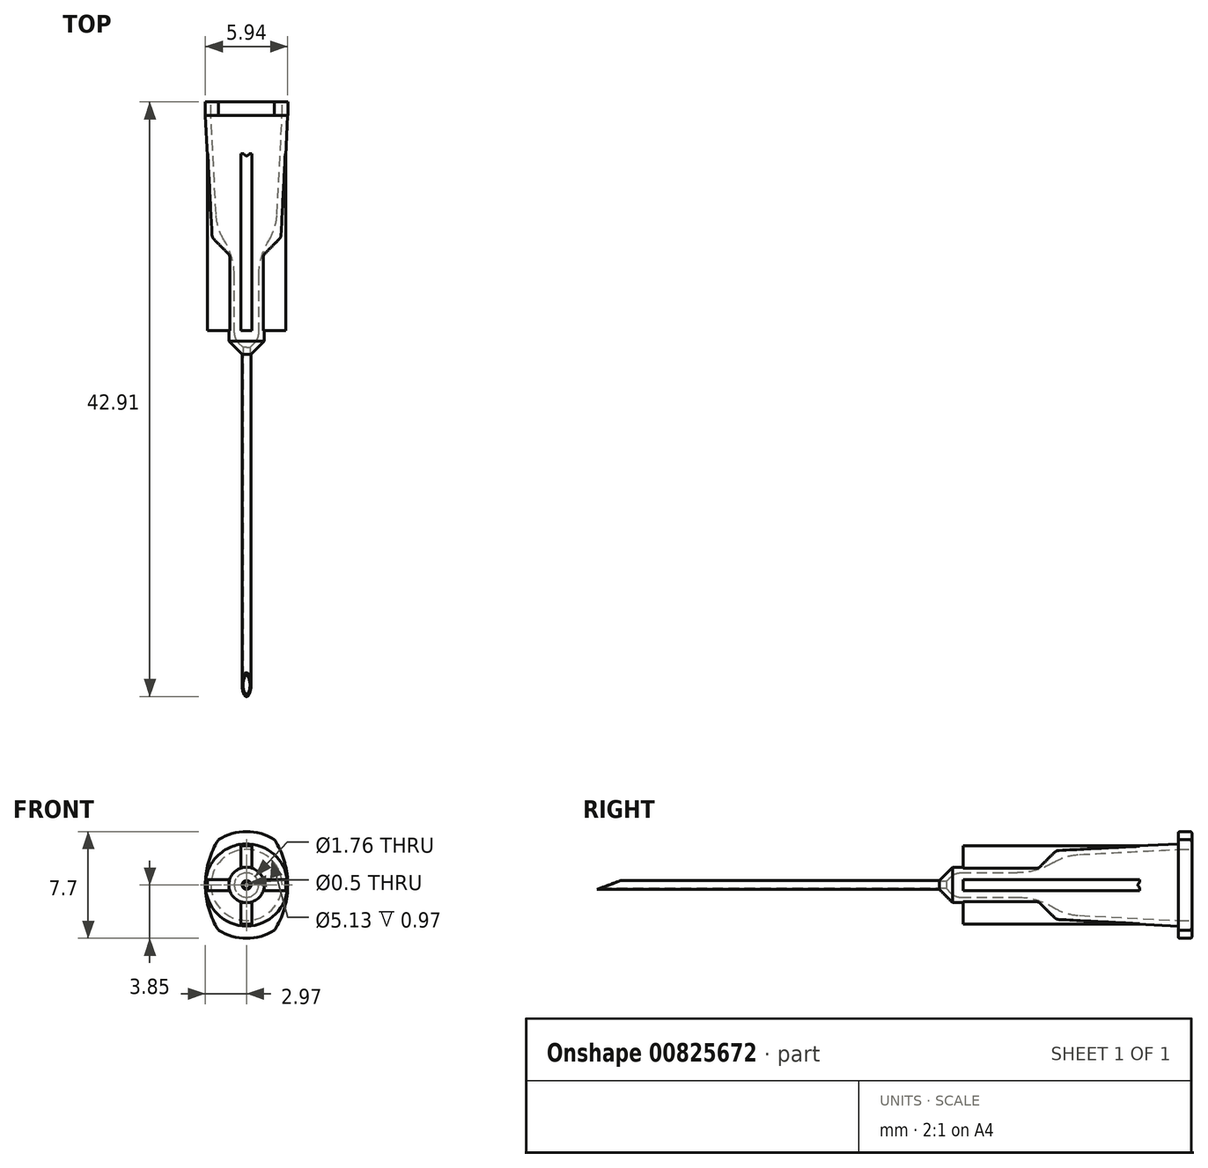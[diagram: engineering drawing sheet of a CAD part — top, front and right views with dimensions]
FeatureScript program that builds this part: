
annotation { "Feature Type Name" : "Feature", "Feature Type Description" : "" }
export const myFeature = defineFeature(function(context is Context, id is Id, definition is map)
    precondition{}
    {
        {
            var Q0;
            Q0=qCreatedBy(makeId("Front.planeOp"),FACE);
            var sketch = newSketch(context, id + "F0", { "sketchPlane" : qUnion([Q0])});
            skCircle(sketch, "E0", {"center": v(0, 0) * mm, "radius": 2.97 * mm});
            skSolve(sketch);
        }
        {
            var Q0;
            Q0=qCreatedBy(makeId("Front.planeOp"),FACE);
            cPlane(context, id + "F1", {"entities" : qUnion([Q0]), "cplaneType" : CPlaneType.OFFSET, "offset" : 8.8 * mm, "width" : 150 * mm, "height" : 150 * mm});
        }
        {
            var Q0;
            Q0=qCreatedBy(id+"F1.planeOp",FACE);
            var sketch = newSketch(context, id + "F2", { "sketchPlane" : qUnion([Q0])});
            skCircle(sketch, "E1", {"center": v(0, 0) * mm, "radius": 2.52 * mm});
            skSolve(sketch);
        }
        {
            var Q0;
            Q0=makeQuery(id+"F0.imprint","IMPRINT",FACE,{"disambiguationData":[TD([[makeQuery(id+"F0.imprint","IMPRINT",EDGE,{"derivedFrom":sQuery(id+"F0.wireOp",EDGE,"E0")}),1.0]])]});
            var Q1;
            Q1=makeQuery(id+"F2.imprint","IMPRINT",FACE,{"disambiguationData":[TD([[makeQuery(id+"F2.imprint","IMPRINT",EDGE,{"derivedFrom":sQuery(id+"F2.wireOp",EDGE,"E1")}),1.0]])]});
            loft(context, id + "F3", {"sheetProfilesArray" : [{ "sheetProfileEntities" : qUnion([Q0]) }, { "sheetProfileEntities" : qUnion([Q1]) }]});
        }
        {
            var Q0;
            Q0=makeQuery(id+"F3.opLoft","CAP_FACE",FACE,{"disambiguationData":[OSD([makeQuery(id+"F2.imprint","IMPRINT",FACE,{"disambiguationData":[TD([[makeQuery(id+"F2.imprint","IMPRINT",EDGE,{"derivedFrom":sQuery(id+"F2.wireOp",EDGE,"E1")}),1.0]])]})])],"isStart":true});
            cPlane(context, id + "F4", {"entities" : qUnion([Q0]), "cplaneType" : CPlaneType.OFFSET, "offset" : 1.28 * mm, "width" : 150 * mm, "height" : 150 * mm});
        }
        {
            var Q0;
            Q0=qCreatedBy(id+"F4.planeOp",FACE);
            var sketch = newSketch(context, id + "F5", { "sketchPlane" : qUnion([Q0])});
            skCircle(sketch, "E2", {"center": v(0, 0) * mm, "radius": 1.28 * mm});
            skSolve(sketch);
        }
        {
            var Q1;
            Q1=makeQuery(id+"F3.opLoft","CAP_FACE",FACE,{"disambiguationData":[OSD([makeQuery(id+"F2.imprint","IMPRINT",FACE,{"disambiguationData":[TD([[makeQuery(id+"F2.imprint","IMPRINT",EDGE,{"derivedFrom":sQuery(id+"F2.wireOp",EDGE,"E1")}),1.0]])]})])],"isStart":true});
            var Q2;
            Q2=makeQuery(id+"F5.imprint","IMPRINT",FACE,{"disambiguationData":[TD([[makeQuery(id+"F5.imprint","IMPRINT",EDGE,{"derivedFrom":sQuery(id+"F5.wireOp",EDGE,"E2")}),1.0]])]});
            loft(context, id + "F6", {"operationType" : NewBodyOperationType.ADD, "sheetProfilesArray" : [{ "sheetProfileEntities" : qUnion([Q1]) }, { "sheetProfileEntities" : qUnion([Q2]) }]});
        }
        {
            var Q0;
            Q0=makeQuery(id+"F6.opLoft","CAP_FACE",FACE,{"disambiguationData":[OSD([makeQuery(id+"F5.imprint","IMPRINT",FACE,{"disambiguationData":[TD([[makeQuery(id+"F5.imprint","IMPRINT",EDGE,{"derivedFrom":sQuery(id+"F5.wireOp",EDGE,"E2")}),1.0]])]})])],"isStart":true});
            extrude(context, id + "F7", {"entities" : qUnion([Q0]), "operationType" : NewBodyOperationType.ADD, "depth" : 6.2 * mm, "offsetDistance" : 25 * mm});
        }
        {
            var Q0;
            Q0=makeQuery(id+"F7.opExtrude","CAP_FACE",FACE,{"disambiguationData":[OSD([makeQuery(id+"F5.imprint","IMPRINT",FACE,{"disambiguationData":[TD([[makeQuery(id+"F5.imprint","IMPRINT",EDGE,{"derivedFrom":sQuery(id+"F5.wireOp",EDGE,"E2")}),1.0]])]})])],"isStart":false});
            var sketch = newSketch(context, id + "F8", { "sketchPlane" : qUnion([Q0])});
            skLineSegment(sketch, "E3.bottom", {"start": v(0.4, 2.82) * mm, "end": v(-0.4, 2.82) * mm});
            skLineSegment(sketch, "E3.left", {"start": v(0.4, 2.82) * mm, "end": v(0.4, 1.22) * mm});
            skLineSegment(sketch, "E3.right", {"start": v(-0.4, 2.82) * mm, "end": v(-0.4, 1.22) * mm});
            skPoint(sketch, "E3.middle", {"position": v(0, 1.28) * mm});
            skArc(sketch, "E4", {"start": v(0.4, 1.22) * mm, "mid": v(0, 1.28) * mm, "end": v(-0.4, 1.22) * mm});
            skLineSegment(sketch, "E5.1.0", {"start": v(-2.82, -0.4) * mm, "end": v(-1.22, -0.4) * mm});
            skLineSegment(sketch, "E5.1.1", {"start": v(-2.82, 0.4) * mm, "end": v(-1.22, 0.4) * mm});
            skLineSegment(sketch, "E5.1.2", {"start": v(-2.82, 0.4) * mm, "end": v(-2.82, -0.4) * mm});
            skArc(sketch, "E5.1.3", {"start": v(-1.22, 0.4) * mm, "mid": v(-1.28, 0) * mm, "end": v(-1.22, -0.4) * mm});
            skLineSegment(sketch, "E5.2.0", {"start": v(0.4, -2.82) * mm, "end": v(0.4, -1.22) * mm});
            skLineSegment(sketch, "E5.2.1", {"start": v(-0.4, -2.82) * mm, "end": v(-0.4, -1.22) * mm});
            skLineSegment(sketch, "E5.2.2", {"start": v(-0.4, -2.82) * mm, "end": v(0.4, -2.82) * mm});
            skArc(sketch, "E5.2.3", {"start": v(-0.4, -1.22) * mm, "mid": v(0, -1.28) * mm, "end": v(0.4, -1.22) * mm});
            skLineSegment(sketch, "E5.3.0", {"start": v(2.82, 0.4) * mm, "end": v(1.22, 0.4) * mm});
            skLineSegment(sketch, "E5.3.1", {"start": v(2.82, -0.4) * mm, "end": v(1.22, -0.4) * mm});
            skLineSegment(sketch, "E5.3.2", {"start": v(2.82, -0.4) * mm, "end": v(2.82, 0.4) * mm});
            skArc(sketch, "E5.3.3", {"start": v(1.22, -0.4) * mm, "mid": v(1.28, 0) * mm, "end": v(1.22, 0.4) * mm});
            skSolve(sketch);
        }
        {
            var Q0;
            Q0 = qSketchRegion(id + "F8", true);
            extrude(context, id + "F9", {"entities" : qUnion([Q0]), "operationType" : NewBodyOperationType.ADD, "oppositeDirection" : true, "depth" : 13.5 * mm, "offsetDistance" : 25 * mm});
        }
        {
            var Q0;
            Q0=makeQuery(id+"F9.boolean.opBoolean","MERGE",FACE,{"derivedFrom":[makeQuery(id+"F7.opExtrude","CAP_FACE",FACE,{"disambiguationData":[OSD([makeQuery(id+"F5.imprint","IMPRINT",FACE,{"disambiguationData":[TD([[makeQuery(id+"F5.imprint","IMPRINT",EDGE,{"derivedFrom":sQuery(id+"F5.wireOp",EDGE,"E2")}),1.0]])]})])],"isStart":false}),makeQuery(id+"F9.opExtrude","CAP_FACE",FACE,{"disambiguationData":[OSD([sQuery(id+"F8.wireOp",EDGE,"E3.bottom"),sQuery(id+"F8.wireOp",EDGE,"E3.left"),sQuery(id+"F8.wireOp",EDGE,"E3.right"),sQuery(id+"F8.wireOp",EDGE,"E4")])],"isStart":true}),makeQuery(id+"F9.opExtrude","CAP_FACE",FACE,{"disambiguationData":[OSD([sQuery(id+"F8.wireOp",EDGE,"E5.1.0"),sQuery(id+"F8.wireOp",EDGE,"E5.1.1"),sQuery(id+"F8.wireOp",EDGE,"E5.1.2"),sQuery(id+"F8.wireOp",EDGE,"E5.1.3")])],"isStart":true}),makeQuery(id+"F9.opExtrude","CAP_FACE",FACE,{"disambiguationData":[OSD([sQuery(id+"F8.wireOp",EDGE,"E5.2.0"),sQuery(id+"F8.wireOp",EDGE,"E5.2.1"),sQuery(id+"F8.wireOp",EDGE,"E5.2.2"),sQuery(id+"F8.wireOp",EDGE,"E5.2.3")])],"isStart":true}),makeQuery(id+"F9.opExtrude","CAP_FACE",FACE,{"disambiguationData":[OSD([sQuery(id+"F8.wireOp",EDGE,"E5.3.0"),sQuery(id+"F8.wireOp",EDGE,"E5.3.1"),sQuery(id+"F8.wireOp",EDGE,"E5.3.2"),sQuery(id+"F8.wireOp",EDGE,"E5.3.3")])],"isStart":true})]});
            var sketch = newSketch(context, id + "F10", { "sketchPlane" : qUnion([Q0])});
            skLineSegment(sketch, "E6", {"start": v(-0.4, 1.22) * mm, "end": v(-0.4, 2.82) * mm});
            skLineSegment(sketch, "E7", {"start": v(-0.4, 2.82) * mm, "end": v(0.4, 2.82) * mm});
            skLineSegment(sketch, "E8", {"start": v(0.4, 2.82) * mm, "end": v(0.4, 1.22) * mm});
            skArc(sketch, "E9", {"start": v(0.4, 1.22) * mm, "mid": v(0, 1.28) * mm, "end": v(-0.4, 1.22) * mm});
            skLineSegment(sketch, "E10.1.0", {"start": v(-1.22, -0.4) * mm, "end": v(-2.82, -0.4) * mm});
            skArc(sketch, "E10.1.1", {"start": v(-1.22, 0.4) * mm, "mid": v(-1.28, 0) * mm, "end": v(-1.22, -0.4) * mm});
            skLineSegment(sketch, "E10.1.2", {"start": v(-2.82, 0.4) * mm, "end": v(-1.22, 0.4) * mm});
            skLineSegment(sketch, "E10.1.3", {"start": v(-2.82, -0.4) * mm, "end": v(-2.82, 0.4) * mm});
            skLineSegment(sketch, "E10.2.0", {"start": v(0.4, -1.22) * mm, "end": v(0.4, -2.82) * mm});
            skArc(sketch, "E10.2.1", {"start": v(-0.4, -1.22) * mm, "mid": v(0, -1.28) * mm, "end": v(0.4, -1.22) * mm});
            skLineSegment(sketch, "E10.2.2", {"start": v(-0.4, -2.82) * mm, "end": v(-0.4, -1.22) * mm});
            skLineSegment(sketch, "E10.2.3", {"start": v(0.4, -2.82) * mm, "end": v(-0.4, -2.82) * mm});
            skLineSegment(sketch, "E10.3.0", {"start": v(1.22, 0.4) * mm, "end": v(2.82, 0.4) * mm});
            skArc(sketch, "E10.3.1", {"start": v(1.22, -0.4) * mm, "mid": v(1.28, 0) * mm, "end": v(1.22, 0.4) * mm});
            skLineSegment(sketch, "E10.3.2", {"start": v(2.82, -0.4) * mm, "end": v(1.22, -0.4) * mm});
            skLineSegment(sketch, "E10.3.3", {"start": v(2.82, 0.4) * mm, "end": v(2.82, -0.4) * mm});
            skSolve(sketch);
        }
        {
            var Q0;
            Q0 = qSketchRegion(id + "F10", true);
            extrude(context, id + "F11", {"entities" : qUnion([Q0]), "operationType" : NewBodyOperationType.REMOVE, "oppositeDirection" : true, "depth" : .75 * mm, "offsetDistance" : 25 * mm});
        }
        {
            var Q0;
            Q0=makeQuery(id+"F9.boolean.opBoolean","MERGE",FACE,{"derivedFrom":[makeQuery(id+"F7.opExtrude","CAP_FACE",FACE,{"disambiguationData":[OSD([makeQuery(id+"F5.imprint","IMPRINT",FACE,{"disambiguationData":[TD([[makeQuery(id+"F5.imprint","IMPRINT",EDGE,{"derivedFrom":sQuery(id+"F5.wireOp",EDGE,"E2")}),1.0]])]})])],"isStart":false}),makeQuery(id+"F9.opExtrude","CAP_FACE",FACE,{"disambiguationData":[OSD([sQuery(id+"F8.wireOp",EDGE,"E3.bottom"),sQuery(id+"F8.wireOp",EDGE,"E3.left"),sQuery(id+"F8.wireOp",EDGE,"E3.right"),sQuery(id+"F8.wireOp",EDGE,"E4")])],"isStart":true}),makeQuery(id+"F9.opExtrude","CAP_FACE",FACE,{"disambiguationData":[OSD([sQuery(id+"F8.wireOp",EDGE,"E5.1.0"),sQuery(id+"F8.wireOp",EDGE,"E5.1.1"),sQuery(id+"F8.wireOp",EDGE,"E5.1.2"),sQuery(id+"F8.wireOp",EDGE,"E5.1.3")])],"isStart":true}),makeQuery(id+"F9.opExtrude","CAP_FACE",FACE,{"disambiguationData":[OSD([sQuery(id+"F8.wireOp",EDGE,"E5.2.0"),sQuery(id+"F8.wireOp",EDGE,"E5.2.1"),sQuery(id+"F8.wireOp",EDGE,"E5.2.2"),sQuery(id+"F8.wireOp",EDGE,"E5.2.3")])],"isStart":true}),makeQuery(id+"F9.opExtrude","CAP_FACE",FACE,{"disambiguationData":[OSD([sQuery(id+"F8.wireOp",EDGE,"E5.3.0"),sQuery(id+"F8.wireOp",EDGE,"E5.3.1"),sQuery(id+"F8.wireOp",EDGE,"E5.3.2"),sQuery(id+"F8.wireOp",EDGE,"E5.3.3")])],"isStart":true})]});
            cPlane(context, id + "F12", {"entities" : qUnion([Q0]), "cplaneType" : CPlaneType.OFFSET, "offset" : .96 * mm, "width" : 150 * mm, "height" : 150 * mm});
        }
        {
            var Q0;
            Q0=qCreatedBy(id+"F12.planeOp",FACE);
            var sketch = newSketch(context, id + "F13", { "sketchPlane" : qUnion([Q0])});
            skCircle(sketch, "E11", {"center": v(0, 0) * mm, "radius": 0.33 * mm});
            skSolve(sketch);
        }
        {
            var Q1;
            Q1=makeQuery(id+"F9.boolean.opBoolean","MERGE",FACE,{"derivedFrom":[makeQuery(id+"F7.opExtrude","CAP_FACE",FACE,{"disambiguationData":[OSD([makeQuery(id+"F5.imprint","IMPRINT",FACE,{"disambiguationData":[TD([[makeQuery(id+"F5.imprint","IMPRINT",EDGE,{"derivedFrom":sQuery(id+"F5.wireOp",EDGE,"E2")}),1.0]])]})])],"isStart":false}),makeQuery(id+"F9.opExtrude","CAP_FACE",FACE,{"disambiguationData":[OSD([sQuery(id+"F8.wireOp",EDGE,"E3.bottom"),sQuery(id+"F8.wireOp",EDGE,"E3.left"),sQuery(id+"F8.wireOp",EDGE,"E3.right"),sQuery(id+"F8.wireOp",EDGE,"E4")])],"isStart":true}),makeQuery(id+"F9.opExtrude","CAP_FACE",FACE,{"disambiguationData":[OSD([sQuery(id+"F8.wireOp",EDGE,"E5.1.0"),sQuery(id+"F8.wireOp",EDGE,"E5.1.1"),sQuery(id+"F8.wireOp",EDGE,"E5.1.2"),sQuery(id+"F8.wireOp",EDGE,"E5.1.3")])],"isStart":true}),makeQuery(id+"F9.opExtrude","CAP_FACE",FACE,{"disambiguationData":[OSD([sQuery(id+"F8.wireOp",EDGE,"E5.2.0"),sQuery(id+"F8.wireOp",EDGE,"E5.2.1"),sQuery(id+"F8.wireOp",EDGE,"E5.2.2"),sQuery(id+"F8.wireOp",EDGE,"E5.2.3")])],"isStart":true}),makeQuery(id+"F9.opExtrude","CAP_FACE",FACE,{"disambiguationData":[OSD([sQuery(id+"F8.wireOp",EDGE,"E5.3.0"),sQuery(id+"F8.wireOp",EDGE,"E5.3.1"),sQuery(id+"F8.wireOp",EDGE,"E5.3.2"),sQuery(id+"F8.wireOp",EDGE,"E5.3.3")])],"isStart":true})]});
            var Q2;
            Q2=makeQuery(id+"F13.imprint","IMPRINT",FACE,{"disambiguationData":[TD([[makeQuery(id+"F13.imprint","IMPRINT",EDGE,{"derivedFrom":sQuery(id+"F13.wireOp",EDGE,"E11")}),1.0]])]});
            loft(context, id + "F14", {"operationType" : NewBodyOperationType.ADD, "sheetProfilesArray" : [{ "sheetProfileEntities" : qUnion([Q1]) }, { "sheetProfileEntities" : qUnion([Q2]) }]});
        }
        {
            var Q0;
            Q0=makeQuery(id+"F3.opLoft","CAP_FACE",FACE,{"disambiguationData":[OSD([makeQuery(id+"F0.imprint","IMPRINT",FACE,{"disambiguationData":[TD([[makeQuery(id+"F0.imprint","IMPRINT",EDGE,{"derivedFrom":sQuery(id+"F0.wireOp",EDGE,"E0")}),1.0]])]})])],"isStart":true});
            shell(context, id + "F15", {"entities" : qUnion([Q0]), "thickness" : .4 * mm});
        }
        {
            var Q0;
            Q0=makeQuery(id+"F14.opLoft","CAP_FACE",FACE,{"disambiguationData":[OSD([makeQuery(id+"F13.imprint","IMPRINT",FACE,{"disambiguationData":[TD([[makeQuery(id+"F13.imprint","IMPRINT",EDGE,{"derivedFrom":sQuery(id+"F13.wireOp",EDGE,"E11")}),1.0]])]})])],"isStart":true});
            extrude(context, id + "F16", {"entities" : qUnion([Q0]), "operationType" : NewBodyOperationType.ADD, "depth" : 24.7 * mm, "offsetDistance" : 25 * mm});
        }
        {
            var Q0;
            Q0=makeQuery(id+"F16.opExtrude","CAP_FACE",FACE,{"disambiguationData":[OSD([makeQuery(id+"F13.imprint","IMPRINT",FACE,{"disambiguationData":[TD([[makeQuery(id+"F13.imprint","IMPRINT",EDGE,{"derivedFrom":sQuery(id+"F13.wireOp",EDGE,"E11")}),1.0]])]})])],"isStart":false});
            var sketch = newSketch(context, id + "F17", { "sketchPlane" : qUnion([Q0])});
            skCircle(sketch, "E12", {"center": v(0, 0) * mm, "radius": 0.25 * mm});
            skSolve(sketch);
        }
        {
            var Q0;
            Q0 = qSketchRegion(id + "F17", true);
            extrude(context, id + "F18", {"entities" : qUnion([Q0]), "operationType" : NewBodyOperationType.REMOVE, "oppositeDirection" : true, "depth" : 55 * mm, "offsetDistance" : 25 * mm});
        }
        {
            var Q0;
            Q0=qCreatedBy(makeId("Right.planeOp"),FACE);
            var sketch = newSketch(context, id + "F19", { "sketchPlane" : qUnion([Q0])});
            skLineSegment(sketch, "E13", {"start": v(-40.1, 0.37) * mm, "end": v(-42.17, 0.37) * mm});
            skLineSegment(sketch, "E14", {"start": v(-42.17, 0.37) * mm, "end": v(-42.17, -0.4) * mm});
            skLineSegment(sketch, "E15", {"start": v(-42.17, -0.4) * mm, "end": v(-40.1, 0.37) * mm});
            skSolve(sketch);
        }
        {
            var Q0;
            Q0=makeQuery(id+"F19.imprint","IMPRINT",FACE,{"disambiguationData":[TD([[makeQuery(id+"F19.imprint","IMPRINT",EDGE,{"derivedFrom":sQuery(id+"F19.wireOp",EDGE,"E13")}),1.0]])]});
            extrude(context, id + "F20", {"entities" : qUnion([Q0]), "operationType" : NewBodyOperationType.REMOVE, "endBound" : BoundingType.SYMMETRIC, "oppositeDirection" : true, "depth" : 25 * mm, "offsetDistance" : 25 * mm});
        }
        {
            var Q0;
            Q0=makeQuery(id+"F3.opLoft","CAP_FACE",FACE,{"disambiguationData":[OSD([makeQuery(id+"F0.imprint","IMPRINT",FACE,{"disambiguationData":[TD([[makeQuery(id+"F0.imprint","IMPRINT",EDGE,{"derivedFrom":sQuery(id+"F0.wireOp",EDGE,"E0")}),1.0]])]})])],"isStart":true});
            var sketch = newSketch(context, id + "F21", { "sketchPlane" : qUnion([Q0])});
            skArc(sketch, "E16", {"start": v(-2.02, -3.27) * mm, "mid": v(0, -3.85) * mm, "end": v(2.02, -3.27) * mm});
            skArc(sketch, "E17.trimOffspring", {"start": v(2.02, 3.27) * mm, "mid": v(0, 3.85) * mm, "end": v(-2.02, 3.27) * mm});
            skArc(sketch, "E18", {"start": v(-2.02, 3.27) * mm, "mid": v(-2.97, 0) * mm, "end": v(-2.02, -3.27) * mm});
            skArc(sketch, "E19.MirrorCS", {"start": v(2.02, 3.27) * mm, "mid": v(2.97, 0) * mm, "end": v(2.02, -3.27) * mm});
            skSolve(sketch);
        }
        {
            var Q0;
            Q0 = qSketchRegion(id + "F21", true);
            extrude(context, id + "F22", {"entities" : qUnion([Q0]), "operationType" : NewBodyOperationType.ADD, "depth" : .97 * mm, "offsetDistance" : 25 * mm});
        }
        {
            var Q0;
            Q0=makeQuery(id+"F22.opExtrude","CAP_FACE",FACE,{"disambiguationData":[OSD([sQuery(id+"F21.wireOp",EDGE,"E16"),sQuery(id+"F21.wireOp",EDGE,"E17.trimOffspring"),sQuery(id+"F21.wireOp",EDGE,"E18"),sQuery(id+"F21.wireOp",EDGE,"E19.MirrorCS")])],"isStart":false});
            var sketch = newSketch(context, id + "F23", { "sketchPlane" : qUnion([Q0])});
            skCircle(sketch, "E20", {"center": v(0, 0) * mm, "radius": 2.56 * mm});
            skSolve(sketch);
        }
        {
            var Q0;
            Q0 = qSketchRegion(id + "F23", true);
            extrude(context, id + "F24", {"entities" : qUnion([Q0]), "operationType" : NewBodyOperationType.REMOVE, "oppositeDirection" : true, "depth" : .97 * mm, "offsetDistance" : 25 * mm});
        }
        {
            var Q0;
            Q0=makeQuery(id+"F22.opExtrude","CAP_EDGE",EDGE,{"disambiguationData":[OSD([sQuery(id+"F21.wireOp",EDGE,"E17.trimOffspring")])],"isStart":false});
            var Q1;
            Q1=makeQuery(id+"F22.opExtrude","CAP_EDGE",EDGE,{"disambiguationData":[OSD([sQuery(id+"F21.wireOp",EDGE,"n3VwcAQu-m9wG-LSh9-epz2-D2UMwBbI9uYN")])],"isStart":false});
            var Q2;
            Q2=makeQuery(id+"F22.opExtrude","CAP_EDGE",EDGE,{"disambiguationData":[OSD([sQuery(id+"F21.wireOp",EDGE,"E16")])],"isStart":false});
            var Q3;
            Q3=makeQuery(id+"F22.opExtrude","CAP_EDGE",EDGE,{"disambiguationData":[OSD([sQuery(id+"F21.wireOp",EDGE,"b956dc51-500c-4db2-886d-4bdfdce920790.MirrorCS")])],"isStart":false});
            fillet(context, id + "F25", {"entities" : qUnion([Q0, Q1, Q2, Q3]), "radius" : .1 * mm, "tangentPropagation" : true, "allowEdgeOverflow" : false});
        }
        {
            var Q0;
            Q0=makeQuery(id+"F22.opExtrude","CAP_EDGE",EDGE,{"disambiguationData":[OSD([sQuery(id+"F21.wireOp",EDGE,"n3VwcAQu-m9wG-LSh9-epz2-D2UMwBbI9uYN")])],"isStart":true});
            var Q1;
            Q1=makeQuery(id+"F22.opExtrude","CAP_EDGE",EDGE,{"disambiguationData":[OSD([sQuery(id+"F21.wireOp",EDGE,"E17.trimOffspring")])],"isStart":true});
            var Q2;
            Q2=makeQuery(id+"F22.opExtrude","CAP_EDGE",EDGE,{"disambiguationData":[OSD([sQuery(id+"F21.wireOp",EDGE,"E16")])],"isStart":true});
            var Q3;
            Q3=makeQuery(id+"F22.opExtrude","CAP_EDGE",EDGE,{"disambiguationData":[OSD([sQuery(id+"F21.wireOp",EDGE,"b956dc51-500c-4db2-886d-4bdfdce920790.MirrorCS")])],"isStart":true});
            fillet(context, id + "F26", {"entities" : qUnion([Q0, Q1, Q2, Q3]), "radius" : .1 * mm, "tangentPropagation" : true, "allowEdgeOverflow" : false});
        }
        {
            var Q0;
            {var subQ0=sQuery(id+"F2.wireOp",EDGE,"E1");Q0=makeQuery(id+"F9.boolean.opBoolean","SPLIT",EDGE,{"disambiguationData":[TD([makeQuery(id+"F9.opExtrude","SWEPT_FACE",FACE,{"disambiguationData":[OSD([sQuery(id+"F8.wireOp",EDGE,"E3.right")])]})])],"derivedFrom":makeQuery(id+"F6.boolean.opBoolean","MERGE",EDGE,{"derivedFrom":[makeQuery(id+"F3.opLoft","MID_CAP_EDGE",EDGE,{"disambiguationData":[OSD([subQ0])],"capPos":1.0}),makeQuery(id+"F6.opLoft","MID_CAP_EDGE",EDGE,{"disambiguationData":[OSD([subQ0])],"capPos":0.0})]})});}
            var Q1;
            {var subQ0=sQuery(id+"F2.wireOp",EDGE,"E1");Q1=makeQuery(id+"F9.boolean.opBoolean","SPLIT",EDGE,{"disambiguationData":[TD([makeQuery(id+"F9.opExtrude","SWEPT_FACE",FACE,{"disambiguationData":[OSD([sQuery(id+"F8.wireOp",EDGE,"E3.left")])]})])],"derivedFrom":makeQuery(id+"F6.boolean.opBoolean","MERGE",EDGE,{"derivedFrom":[makeQuery(id+"F3.opLoft","MID_CAP_EDGE",EDGE,{"disambiguationData":[OSD([subQ0])],"capPos":1.0}),makeQuery(id+"F6.opLoft","MID_CAP_EDGE",EDGE,{"disambiguationData":[OSD([subQ0])],"capPos":0.0})]})});}
            var Q2;
            {var subQ0=sQuery(id+"F2.wireOp",EDGE,"E1");Q2=makeQuery(id+"F9.boolean.opBoolean","SPLIT",EDGE,{"disambiguationData":[TD([makeQuery(id+"F9.opExtrude","SWEPT_FACE",FACE,{"disambiguationData":[OSD([sQuery(id+"F8.wireOp",EDGE,"E5.2.0")])]})])],"derivedFrom":makeQuery(id+"F6.boolean.opBoolean","MERGE",EDGE,{"derivedFrom":[makeQuery(id+"F3.opLoft","MID_CAP_EDGE",EDGE,{"disambiguationData":[OSD([subQ0])],"capPos":1.0}),makeQuery(id+"F6.opLoft","MID_CAP_EDGE",EDGE,{"disambiguationData":[OSD([subQ0])],"capPos":0.0})]})});}
            var Q3;
            {var subQ0=sQuery(id+"F2.wireOp",EDGE,"E1");Q3=makeQuery(id+"F9.boolean.opBoolean","SPLIT",EDGE,{"disambiguationData":[TD([makeQuery(id+"F9.opExtrude","SWEPT_FACE",FACE,{"disambiguationData":[OSD([sQuery(id+"F8.wireOp",EDGE,"E5.1.0")])]})])],"derivedFrom":makeQuery(id+"F6.boolean.opBoolean","MERGE",EDGE,{"derivedFrom":[makeQuery(id+"F3.opLoft","MID_CAP_EDGE",EDGE,{"disambiguationData":[OSD([subQ0])],"capPos":1.0}),makeQuery(id+"F6.opLoft","MID_CAP_EDGE",EDGE,{"disambiguationData":[OSD([subQ0])],"capPos":0.0})]})});}
            fillet(context, id + "F27", {"entities" : qUnion([Q0, Q1, Q2, Q3]), "radius" : .5 * mm, "tangentPropagation" : true, "allowEdgeOverflow" : false});
        }
        {
            var Q0;
            {var subQ0=sQuery(id+"F5.wireOp",EDGE,"E2");Q0=makeQuery(id+"F9.boolean.opBoolean","SPLIT",EDGE,{"disambiguationData":[TD([makeQuery(id+"F9.opExtrude","SWEPT_FACE",FACE,{"disambiguationData":[OSD([sQuery(id+"F8.wireOp",EDGE,"E5.1.0")])]})])],"derivedFrom":makeQuery(id+"F7.boolean.opBoolean","MERGE",EDGE,{"derivedFrom":[makeQuery(id+"F6.opLoft","MID_CAP_EDGE",EDGE,{"disambiguationData":[OSD([subQ0])],"capPos":1.0}),makeQuery(id+"F7.opExtrude","CAP_EDGE",EDGE,{"disambiguationData":[OSD([subQ0])],"isStart":true})]})});}
            var Q1;
            {var subQ0=sQuery(id+"F5.wireOp",EDGE,"E2");Q1=makeQuery(id+"F9.boolean.opBoolean","SPLIT",EDGE,{"disambiguationData":[TD([makeQuery(id+"F9.opExtrude","SWEPT_FACE",FACE,{"disambiguationData":[OSD([sQuery(id+"F8.wireOp",EDGE,"E5.2.0")])]})])],"derivedFrom":makeQuery(id+"F7.boolean.opBoolean","MERGE",EDGE,{"derivedFrom":[makeQuery(id+"F6.opLoft","MID_CAP_EDGE",EDGE,{"disambiguationData":[OSD([subQ0])],"capPos":1.0}),makeQuery(id+"F7.opExtrude","CAP_EDGE",EDGE,{"disambiguationData":[OSD([subQ0])],"isStart":true})]})});}
            var Q2;
            {var subQ0=sQuery(id+"F5.wireOp",EDGE,"E2");Q2=makeQuery(id+"F9.boolean.opBoolean","SPLIT",EDGE,{"disambiguationData":[TD([makeQuery(id+"F9.opExtrude","SWEPT_FACE",FACE,{"disambiguationData":[OSD([sQuery(id+"F8.wireOp",EDGE,"E3.left")])]})])],"derivedFrom":makeQuery(id+"F7.boolean.opBoolean","MERGE",EDGE,{"derivedFrom":[makeQuery(id+"F6.opLoft","MID_CAP_EDGE",EDGE,{"disambiguationData":[OSD([subQ0])],"capPos":1.0}),makeQuery(id+"F7.opExtrude","CAP_EDGE",EDGE,{"disambiguationData":[OSD([subQ0])],"isStart":true})]})});}
            var Q3;
            {var subQ0=sQuery(id+"F5.wireOp",EDGE,"E2");Q3=makeQuery(id+"F9.boolean.opBoolean","SPLIT",EDGE,{"disambiguationData":[TD([makeQuery(id+"F9.opExtrude","SWEPT_FACE",FACE,{"disambiguationData":[OSD([sQuery(id+"F8.wireOp",EDGE,"E3.right")])]})])],"derivedFrom":makeQuery(id+"F7.boolean.opBoolean","MERGE",EDGE,{"derivedFrom":[makeQuery(id+"F6.opLoft","MID_CAP_EDGE",EDGE,{"disambiguationData":[OSD([subQ0])],"capPos":1.0}),makeQuery(id+"F7.opExtrude","CAP_EDGE",EDGE,{"disambiguationData":[OSD([subQ0])],"isStart":true})]})});}
            fillet(context, id + "F28", {"entities" : qUnion([Q0, Q1, Q2, Q3]), "radius" : .3 * mm, "tangentPropagation" : true, "allowEdgeOverflow" : false});
        }
        {
            var Q0;
            Q0=makeQuery(id+"F15.opShell","OFFSET_EDGE",EDGE,{"disambiguationData":[OSD([sQuery(id+"F2.wireOp",EDGE,"E1")])]});
            fillet(context, id + "F29", {"entities" : qUnion([Q0]), "radius" : 4 * mm, "tangentPropagation" : true, "allowEdgeOverflow" : false});
        }
        {
            var Q0;
            Q0=makeQuery(id+"F15.opShell","OFFSET_EDGE",EDGE,{"disambiguationData":[OSD([sQuery(id+"F5.wireOp",EDGE,"E2")])]});
            fillet(context, id + "F30", {"entities" : qUnion([Q0]), "radius" : 5 * mm, "tangentPropagation" : true, "allowEdgeOverflow" : false});
        }
        {
            var Q0;
            Q0=makeQuery(id+"F15.opShell","OFFSET_EDGE",EDGE,{"disambiguationData":[OSD([sQuery(id+"F5.wireOp",EDGE,"E2"),sQuery(id+"F10.wireOp",EDGE,"E9"),sQuery(id+"F10.wireOp",EDGE,"E10.1.1"),sQuery(id+"F10.wireOp",EDGE,"E10.2.1"),sQuery(id+"F10.wireOp",EDGE,"E10.3.1")])]});
            fillet(context, id + "F31", {"entities" : qUnion([Q0]), "radius" : 1 * mm, "tangentPropagation" : true, "allowEdgeOverflow" : false});
        }
    });
